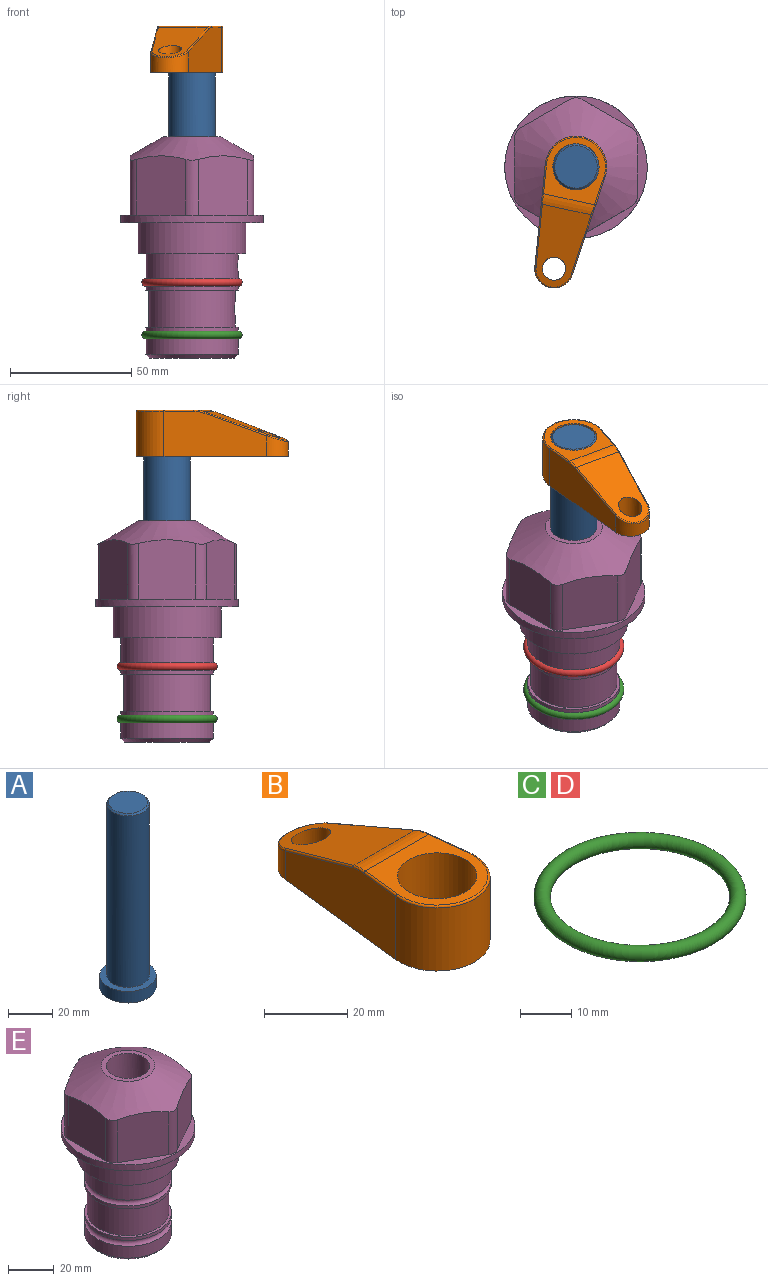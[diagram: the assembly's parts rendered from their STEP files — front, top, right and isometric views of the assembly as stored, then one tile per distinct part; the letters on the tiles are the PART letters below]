
ASSEMBLY  parts=5 mates=3
PART A: 6 faces, bbox 25.4x25.4x101.6 mm
  f0: plane 17.46x17.46mm, normal (0,0,1), area 239.5mm2, adj f5
  f1: plane 25.4x25.4mm, normal (0,0,-1), area 506.7mm2, adj f2
  f2: cylinder r=12.7mm len=25.4mm, axis (0,0,1), area 506.7mm2, adj f1,f3
  f3: plane 25.4x25.4mm, normal (0,0,1), area 221.7mm2, adj f2,f4
  f4: cylinder r=9.53mm len=94.46mm, axis (0,0,1), area 5653mm2, adj f3,f5
  f5: cone r=8.73mm half-angle=45deg, axis (0,0,-1), area 64.4mm2, adj f0,f4
PART B: 44 faces, bbox 27.5x64.5x19.1 mm
  f0: plane 2.3x0.95mm, normal (0,0,-1), area 1mm2, adj f25,f30,f34
  f1: plane 63.5x25.4mm, normal (0,0,-1), area 561.7mm2, adj f2,f3,f4,f5,f6,f7,f19,f20
  f2: cylinder r=12.7mm len=25.4mm, axis (0,0,-1), area 792.2mm2, adj f1,f3,f5,f13
  f3: plane 42.33x18.54mm, normal (0.99,0.11,0), area 647mm2, adj f1,f2,f4,f11,f12,f14
  f4: cylinder r=7.94mm len=15.78mm, axis (0,0,-1), area 158.6mm2, adj f1,f3,f5,f16
  f5: plane 42.33x18.54mm, normal (-0.99,0.11,0), area 647mm2, adj f1,f2,f4,f15,f17,f18
  f6: cylinder r=9.53mm len=19.05mm, axis (0,0,-1), area 1140.1mm2, adj f1,f8
  f7: cylinder r=4.76mm len=10.98mm, axis (0,0,-1), area 276.1mm2, adj f1,f9
  f8: plane 25.83x24.38mm, normal (0,0,1), area 262.2mm2, adj f6,f10,f11,f13,f15
  f9: plane 32.49x20.55mm, normal (0,0.34,0.94), area 489.9mm2, adj f7,f10,f14,f16,f18
  f10: cylinder r=12.7mm len=21.49mm, axis (-1,0,0), area 93.2mm2, adj f8,f9,f12,f17
  f11: cylinder r=0.51mm len=12.34mm, axis (0.11,-0.99,0), area 9.9mm2, adj f3,f8,f12,f13
  f12: bspline ~7.62x1.64mm, area 3.5mm2, adj f3,f10,f11,f14
  f13: torus R=12.19mm, axis (0,0,1), area 33.6mm2, adj f2,f8,f11,f15
  f14: cylinder r=0.51mm len=26.01mm, axis (0.1,-0.93,0.34), area 21.6mm2, adj f3,f9,f12,f16
  f15: cylinder r=0.51mm len=12.34mm, axis (0.11,0.99,0), area 9.9mm2, adj f5,f8,f13,f17
  f16: bspline ~15.78x7.05mm, area 15.7mm2, adj f4,f9,f14,f18
  f17: bspline ~7.62x1.64mm, area 3.5mm2, adj f5,f10,f15,f18
  f18: cylinder r=0.51mm len=26.01mm, axis (0.1,0.93,-0.34), area 21.6mm2, adj f5,f9,f16,f17
  f19: plane 21.6x14.29mm, normal (-0.99,-0.11,0), area 242.6mm2, adj f1,f26,f28,f34,f36,f38
  f20: plane 21.6x14.29mm, normal (0.99,-0.11,0), area 242.6mm2, adj f1,f27,f29,f37,f39,f41
  f21: cylinder r=12.7mm len=14.29mm, axis (0,0,-1), area 173.2mm2, adj f1,f26,f27,f30,f31,f33
  f22: cylinder r=7.94mm len=7.63mm, axis (0,0,-1), area 53.8mm2, adj f1,f28,f29,f42
  f23: plane 2.3x0.95mm, normal (0,0,-1), area 1mm2, adj f25,f33,f37
  f24: plane 17.94x12.32mm, normal (0,-0.34,-0.94), area 191.2mm2, adj f25,f38,f41,f42
  f25: cylinder r=9.53mm len=12.93mm, axis (-1,0,0), area 37.5mm2, adj f0,f23,f24,f31,f36,f39
  f26: cylinder r=1.59mm len=14.29mm, axis (0,0,-1), area 49mm2, adj f1,f19,f21,f32
  f27: cylinder r=1.59mm len=14.29mm, axis (0,0,-1), area 49mm2, adj f1,f20,f21,f35
  f28: cylinder r=1.59mm len=7.28mm, axis (0,0,-1), area 22.1mm2, adj f1,f19,f22,f40
  f29: cylinder r=1.59mm len=7.28mm, axis (0,0,-1), area 22.1mm2, adj f1,f20,f22,f43
  f30: torus R=14.29mm, axis (0,0,1), area 5.8mm2, adj f0,f21,f31,f32
  f31: bspline ~11.06x2.73mm, area 20.8mm2, adj f21,f25,f30,f33
  f32: sphere r=1.59mm, area 5.4mm2, adj f26,f30,f34
  f33: torus R=14.29mm, axis (0,0,1), area 5.8mm2, adj f21,f23,f31,f35
  f34: cylinder r=1.59mm len=1.68mm, axis (-0.11,0.99,0), area 2.4mm2, adj f0,f19,f32,f36
  f35: sphere r=1.59mm, area 5.4mm2, adj f27,f33,f37
  f36: bspline ~5.82x2.33mm, area 7.7mm2, adj f19,f25,f34,f38
  f37: cylinder r=1.59mm len=1.68mm, axis (0.11,0.99,0), area 2.4mm2, adj f20,f23,f35,f39
  f38: cylinder r=1.59mm len=18.33mm, axis (0.1,-0.93,0.34), area 46.7mm2, adj f19,f24,f36,f40
  f39: bspline ~5.82x2.33mm, area 7.7mm2, adj f20,f25,f37,f41
  f40: sphere r=1.59mm, area 3.6mm2, adj f28,f38,f42
  f41: cylinder r=1.59mm len=18.33mm, axis (0.1,0.93,-0.34), area 46.7mm2, adj f20,f24,f39,f43
  f42: bspline ~8.31x1.84mm, area 15.3mm2, adj f22,f24,f40,f43
  f43: sphere r=1.59mm, area 3.6mm2, adj f29,f41,f42
PART C: 1 faces, bbox 44.7x44.7x3.2 mm
  f0: torus R=19.05mm, axis (0,0,1), area 1193.9mm2
PART D: same geometry as C
PART E: 36 faces, bbox 58.7x58.7x91.2 mm
  f0: cylinder r=17.78mm len=35.56mm, axis (0,0,1), area 1670.8mm2, adj f23,f24,f31
  f1: cylinder r=19.05mm len=38.1mm, axis (0,0,1), area 1191.9mm2, adj f26,f27,f30
  f2: plane 58.66x58.66mm, normal (0,0,-1), area 1150.6mm2, adj f3,f28
  f3: cylinder r=29.33mm len=58.66mm, axis (0,0,-1), area 585.1mm2, adj f2,f4
  f4: plane 58.66x58.66mm, normal (0,0,1), area 475.9mm2, adj f3,f5,f6,f7,f8,f9,f10,f11
  f5: plane 24.5x20.32mm, normal (-0.5,0.87,0), area 562.8mm2, adj f4,f15,f16,f17
  f6: plane 24.5x20.32mm, normal (0.5,0.87,0), area 562.8mm2, adj f4,f14,f15,f17
  f7: plane 24.5x23.48mm, normal (1,0,0), area 562.8mm2, adj f4,f13,f14,f17
  f8: plane 24.5x20.32mm, normal (0.5,-0.87,0), area 562.8mm2, adj f4,f12,f13,f17
  f9: plane 24.5x20.32mm, normal (-0.5,-0.87,0), area 562.8mm2, adj f4,f11,f12,f17
  f10: plane 24.5x23.48mm, normal (-1,0,0), area 562.8mm2, adj f4,f11,f16,f17
  f11: cylinder r=5.08mm len=23.01mm, axis (0,0,-1), area 121.2mm2, adj f4,f9,f10,f17
  f12: cylinder r=5.08mm len=23.01mm, axis (0,0,-1), area 121.2mm2, adj f4,f8,f9,f17
  f13: cylinder r=5.08mm len=23.01mm, axis (0,0,-1), area 121.2mm2, adj f4,f7,f8,f17
  f14: cylinder r=5.08mm len=23.01mm, axis (0,0,-1), area 121.2mm2, adj f4,f6,f7,f17
  f15: cylinder r=5.08mm len=23.01mm, axis (0,0,-1), area 121.2mm2, adj f4,f5,f6,f17
  f16: cylinder r=5.08mm len=23.01mm, axis (0,0,-1), area 121.2mm2, adj f4,f5,f10,f17
  f17: cone r=11.73mm half-angle=60deg, axis (0,0,-1), area 2071.8mm2, adj f5,f6,f7,f8,f9,f10,f11,f12
  f18: plane 23.46x23.46mm, normal (0,0,1), area 147.4mm2, adj f17,f35
  f19: plane 34.93x34.93mm, normal (0,0,-1), area 958mm2, adj f29
  f20: cylinder r=19.05mm len=38.1mm, axis (0,0,1), area 760.1mm2, adj f21,f29
  f21: torus R=19.05mm, axis (0,0,1), area 565.3mm2, adj f20,f22
  f22: cylinder r=19.05mm len=38.1mm, axis (0,0,1), area 190mm2, adj f21,f23
  f23: plane 38.1x38.1mm, normal (0,0,1), area 146.9mm2, adj f0,f22
  f24: plane 38.1x38.1mm, normal (0,0,-1), area 146.9mm2, adj f0,f25
  f25: cylinder r=19.05mm len=38.1mm, axis (0,0,1), area 190mm2, adj f24,f26
  f26: torus R=19.05mm, axis (0,0,1), area 565.3mm2, adj f1,f25
  f27: plane 44.45x44.45mm, normal (0,0,-1), area 411.7mm2, adj f1,f28
  f28: cylinder r=22.23mm len=44.45mm, axis (0,0,1), area 1773.5mm2, adj f2,f27
  f29: cone r=19.05mm half-angle=45deg, axis (0,0,1), area 257.5mm2, adj f19,f20
  f30: cylinder r=3.17mm len=6.75mm, axis (-1,0,0), area 128mm2, adj f1,f33
  f31: cylinder r=3.17mm len=6.35mm, axis (-1,0,0), area 102.5mm2, adj f0,f33
  f32: plane 25.4x25.4mm, normal (0,0,1), area 506.7mm2, adj f33
  f33: cylinder r=12.7mm len=66.42mm, axis (0,0,-1), area 5236.2mm2, adj f30,f31,f32,f34
  f34: cone r=9.53mm half-angle=30deg, axis (0,0,-1), area 443.4mm2, adj f33,f35
  f35: cylinder r=9.53mm len=19.05mm, axis (0,0,-1), area 849mm2, adj f18,f34
PLACE A rot(axis=(0,0,-1),102.2deg) t=(0,0,7.45)mm
PLACE B rot(axis=(0,0,1),167.8deg) t=(0,0,62.06)mm
PLACE C t=(0,0,-21.59)mm
PLACE D at identity
PLACE E at identity fixed
MATE fastened C.f0 <-> E.f0  axis (0,0,1) through (0,0,-46.1)mm
MATE cylindrical A.f2 <-> E.f0  axis (0,0,1) through (0,0,33.09)mm
MATE fastened B.f2 <-> A.f2  axis (0,0,1) through (0,0,81.11)mm
